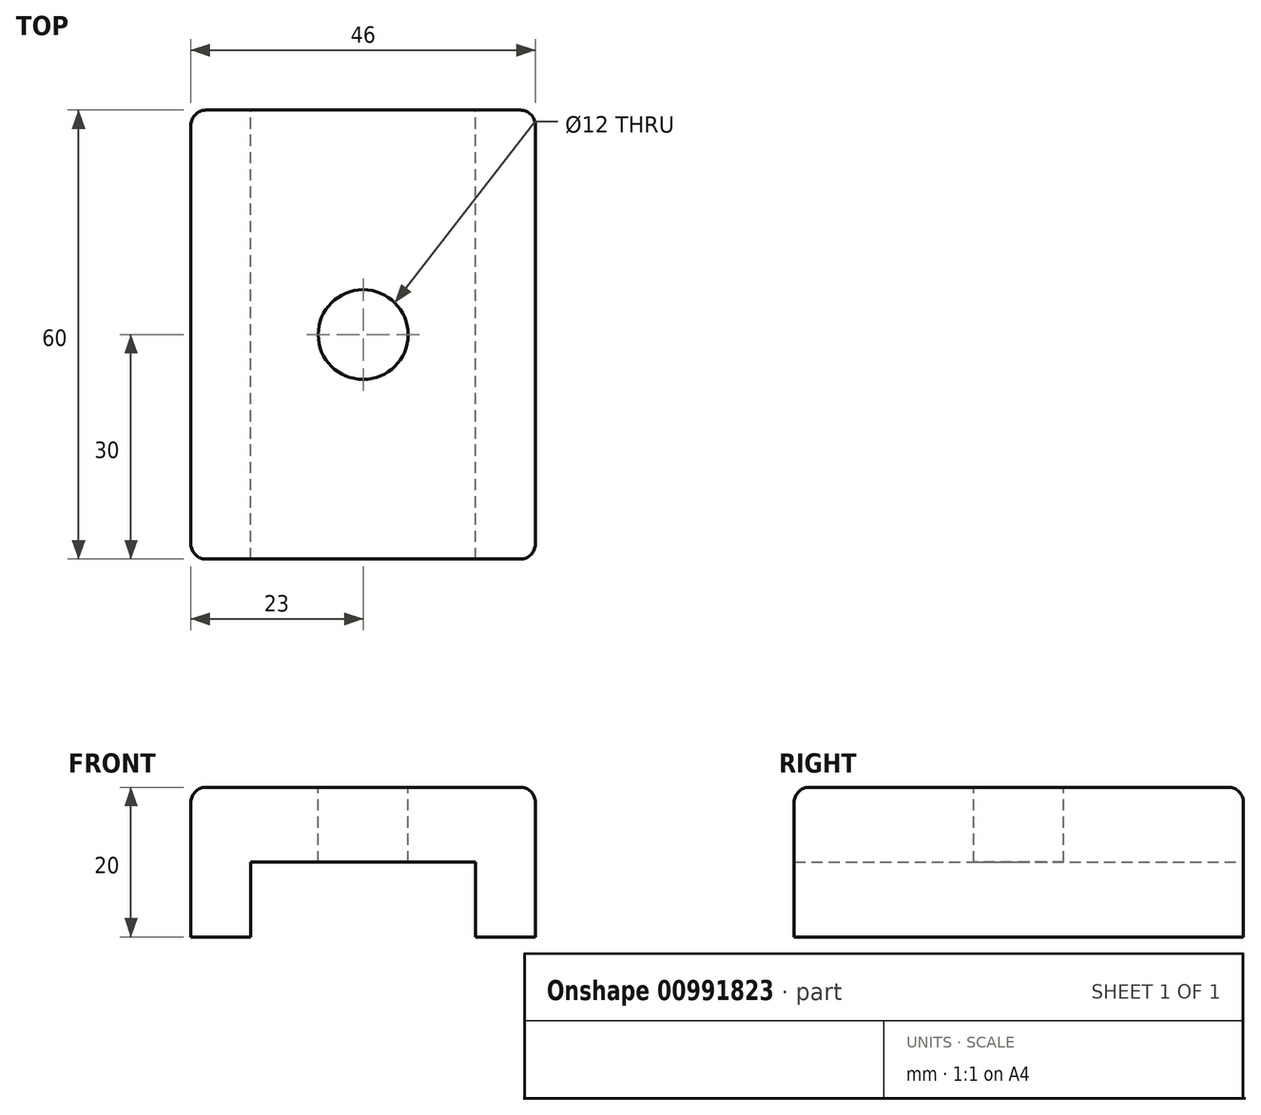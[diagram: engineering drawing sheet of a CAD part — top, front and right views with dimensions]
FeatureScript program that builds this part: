
annotation { "Feature Type Name" : "Feature", "Feature Type Description" : "" }
export const myFeature = defineFeature(function(context is Context, id is Id, definition is map)
    precondition{}
    {
        {
            var Q0;
            Q0=qCreatedBy(makeId("Front.planeOp"),FACE);
            var sketch = newSketch(context, id + "F0", { "sketchPlane" : qUnion([Q0])});
            skLineSegment(sketch, "E0.bottom", {"start": v(-23, -10) * mm, "end": v(-15, -10) * mm});
            skLineSegment(sketch, "E0.top", {"start": v(-23, 10) * mm, "end": v(23, 10) * mm});
            skLineSegment(sketch, "E0.left", {"start": v(-23, -10) * mm, "end": v(-23, 10) * mm});
            skLineSegment(sketch, "E0.right", {"start": v(23, -10) * mm, "end": v(23, 10) * mm});
            skPoint(sketch, "E0.middle", {"position": v(0, 0) * mm});
            skLineSegment(sketch, "E1.top", {"start": v(-15, 0) * mm, "end": v(15, 0) * mm});
            skLineSegment(sketch, "E1.left", {"start": v(-15, -10) * mm, "end": v(-15, 0) * mm});
            skLineSegment(sketch, "E1.right", {"start": v(15, -10) * mm, "end": v(15, 0) * mm});
            skLineSegment(sketch, "E2.trimOffspring", {"start": v(15, -10) * mm, "end": v(23, -10) * mm});
            skSolve(sketch);
        }
        {
            var Q0;
            Q0 = qSketchRegion(id + "F0", true);
            extrude(context, id + "F1", {"entities" : qUnion([Q0]), "depth" : 60 * mm, "offsetDistance" : 25 * mm});
        }
        {
            var Q0;
            Q0=makeQuery(id+"F1.opExtrude","SWEPT_FACE",FACE,{"disambiguationData":[OSD([sQuery(id+"F0.wireOp",EDGE,"E0.top")])]});
            var sketch = newSketch(context, id + "F2", { "sketchPlane" : qUnion([Q0])});
            skCircle(sketch, "E3", {"center": v(0, -30) * mm, "radius": 6 * mm});
            skPoint(sketch, "E3.centerSnap0", {"position": v(23, -30) * mm});
            skSolve(sketch);
        }
        {
            var Q0;
            Q0 = qSketchRegion(id + "F2", true);
            extrude(context, id + "F3", {"entities" : qUnion([Q0]), "operationType" : NewBodyOperationType.REMOVE, "oppositeDirection" : true, "depth" : 25 * mm, "offsetDistance" : 25 * mm});
        }
        {
            var Q0;
            Q0=makeQuery(id+"F1.opExtrude","CAP_EDGE",EDGE,{"disambiguationData":[OSD([sQuery(id+"F0.wireOp",EDGE,"E0.top")])],"isStart":true});
            var Q1;
            Q1=makeQuery(id+"F1.opExtrude","CAP_EDGE",EDGE,{"disambiguationData":[OSD([sQuery(id+"F0.wireOp",EDGE,"E0.right")])],"isStart":true});
            var Q2;
            Q2=makeQuery(id+"F1.opExtrude","CAP_EDGE",EDGE,{"disambiguationData":[OSD([sQuery(id+"F0.wireOp",EDGE,"E0.left")])],"isStart":true});
            var Q3;
            Q3=makeQuery(id+"F1.opExtrude","CAP_EDGE",EDGE,{"disambiguationData":[OSD([sQuery(id+"F0.wireOp",EDGE,"E0.left")])],"isStart":false});
            var Q4;
            Q4=makeQuery(id+"F1.opExtrude","SWEPT_EDGE",EDGE,{"disambiguationData":[OSD([sQuery(id+"F0.wireOp",EDGE,"E0.top"),sQuery(id+"F0.wireOp",EDGE,"E0.left")])]});
            var Q5;
            Q5=makeQuery(id+"F1.opExtrude","CAP_EDGE",EDGE,{"disambiguationData":[OSD([sQuery(id+"F0.wireOp",EDGE,"E0.top")])],"isStart":false});
            var Q6;
            Q6=makeQuery(id+"F1.opExtrude","SWEPT_EDGE",EDGE,{"disambiguationData":[OSD([sQuery(id+"F0.wireOp",EDGE,"E0.top"),sQuery(id+"F0.wireOp",EDGE,"E0.right")])]});
            var Q7;
            Q7=makeQuery(id+"F1.opExtrude","CAP_EDGE",EDGE,{"disambiguationData":[OSD([sQuery(id+"F0.wireOp",EDGE,"E0.right")])],"isStart":false});
            fillet(context, id + "F4", {"entities" : qUnion([Q0, Q1, Q2, Q3, Q4, Q5, Q6, Q7]), "radius" : 2 * mm, "tangentPropagation" : true, "allowEdgeOverflow" : false});
        }
    });
